# Revit family: Bed_Pan-American_Standard-Cleanser-7880.124xxx
name_source: partatom
category: Plumbing Fixtures
revit_build: Autodesk Revit 2014 (Build: 20130308_1515(x64)
units: mm (PartAtom-declared; Revit-internal decimal feet)

## types (1)
- 7880.124
    Assembly Code = D2030400
    CW Connection = Yes
    CWFU = 1.5
    Default Elevation = 1' - 5 1/4"
    Description = Bed Pan Cleaners Self-Closing Spray and Wall Mounted Pedal Valve.
    HW Connection = Yes
    HWFU = 1.5
    Height = 1' - 10 1/4"
    Inlet Diameter Connection = 0' - 0 3/8"
    Length = 0' - 11 5/16"
    Manufacturer = American Standard
    Material = Brass-American Standard-002-Polished Chrome
    Model = 7880.124
    NPT Connection Size = 0' - 0 1/2"
    Outlet Diameter = 0' - 0 3/8"
    Product Documentation Link = https://www.americanstandard-us.com
    Product Page URL = https://www.americanstandard-us.com
    Revised Date = 11/21/2016
    URL = https://www.americanstandard-us.com
    Vent Connection = No
    WFU = 2
    Waste Connection = Yes
    Width = 0' - 3 3/4"

## geometry (parser evidence)
native form markers: Sweep x2
no freeform markers — native parametric forms only
